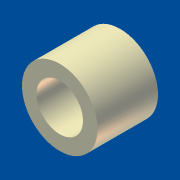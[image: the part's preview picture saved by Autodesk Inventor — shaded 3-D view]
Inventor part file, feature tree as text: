
AUTODESK INVENTOR PART (.ipt)
format: ipt  version: 2012 SP1 (Build 160190100, 190)  size: 98,816 bytes
history: native  units: in
note: dims shown in document units (in); Inventor stores cm internally (conversion verified against a paired STEP export)
features: imported_body x1, extrude x1, sketch x1
ambient origin geometry x8: Origin, YZ Plane, XZ Plane, XY Plane, X Axis, Y Axis, Z Axis, Center Point
bodies: Solid1 (feature_tree)
feature tree (3):
  imported_body  "Base1"
  extrude  "Extrusion1"  [1 undecoded]
  sketch  "Sketch1"  dims[d0=0.125in d1=0.0in]
note: 1 required parameter value undecoded (feature->parameter linkage not recoverable at this tier; creation-order binding heuristic only, values carry confidence <= 0.55)
